# Revit family: Legrand_Gestion_Numerique_Batiment_LIGHTUP_Donnees
name_source: partatom
category: Dispositifs de données
units: mm (PartAtom-declared; Revit-internal decimal feet)

## family parameters
Conserver l'orientation des annotations = Non
Cote de connecteur circulaire = Utiliser le diamètre
Couper avec des vides une fois chargée = Non
Hôte = Face
Numéro OmniClass = 23.85.50.17
Partagée = Non
Repere pour localisation dans la piece = Non
Titre OmniClass = Communication and Data Processing Equipment
Type d'élément = Normal

## types (1)
- MULTI CAPTEURS ACTIVITE
    Bluetooth BLE = Oui
    Classe ETIM = EC001582-Détecteur de mouvement pour systèmes de bus
    Classe POE = Class1
    Code EAN = 3414972281133
    Conditions Générale d'Utilisation = https://export.legrand.com
    Couleur = Blanc
    Description = Détecteur multi-capteurs d'activités Light Up, mesures environementales et comptage de personnes
    Distance paramétrable = Oui
    Désignation produit = MULTI CAPTEURS ACTIVITE
    Détection de forme = rectangulaire
    Détection de surface = 64m2
    Elévation par défaut = 1219 mm
    Etiquette_ZD_ZS_ACTIVITY_ADVANCED = Oui
    Fabricant = LEGRAND
    Famille imbriquée = ACTIVITY_SENSOR
    Hauteur = 47 mm
    Hauteur Optimale = 2600 mm
    Hauteur de pose (Min-Max) = 2400-4000
    Hauteur_Saillie = 93 mm  [stored 0.305118 ft]
    IK = 04
    IP = 20
    Largeur = 103 mm
    Longueur = 157 mm
    Mode de pose = En saillie et encastré
    Modèle Produit = detecteur de presence
    Norme POE = 802.3af
    Poids = 241 g
    Profondeur = 40 mm  [stored 0.131234 ft]
    Protocole de Communication = Applicatif HTTPS,MQTT,MQTTS
    Référence / Modèle = 048591
    Temperature d'utilisation MIN-MAX = +5°C / +30 °C
    Type de capteur = caméra thermique
    URL = https://www.legrand.fr
    Wifi = Oui
    Zigbee = Non
    Zones = ZD_ACTIVITY_ADVANCED
    Zones Configurables = Oui

note: [stored X ft] marks values corroborated as IEEE doubles in the binary element streams (Revit-internal decimal feet)
